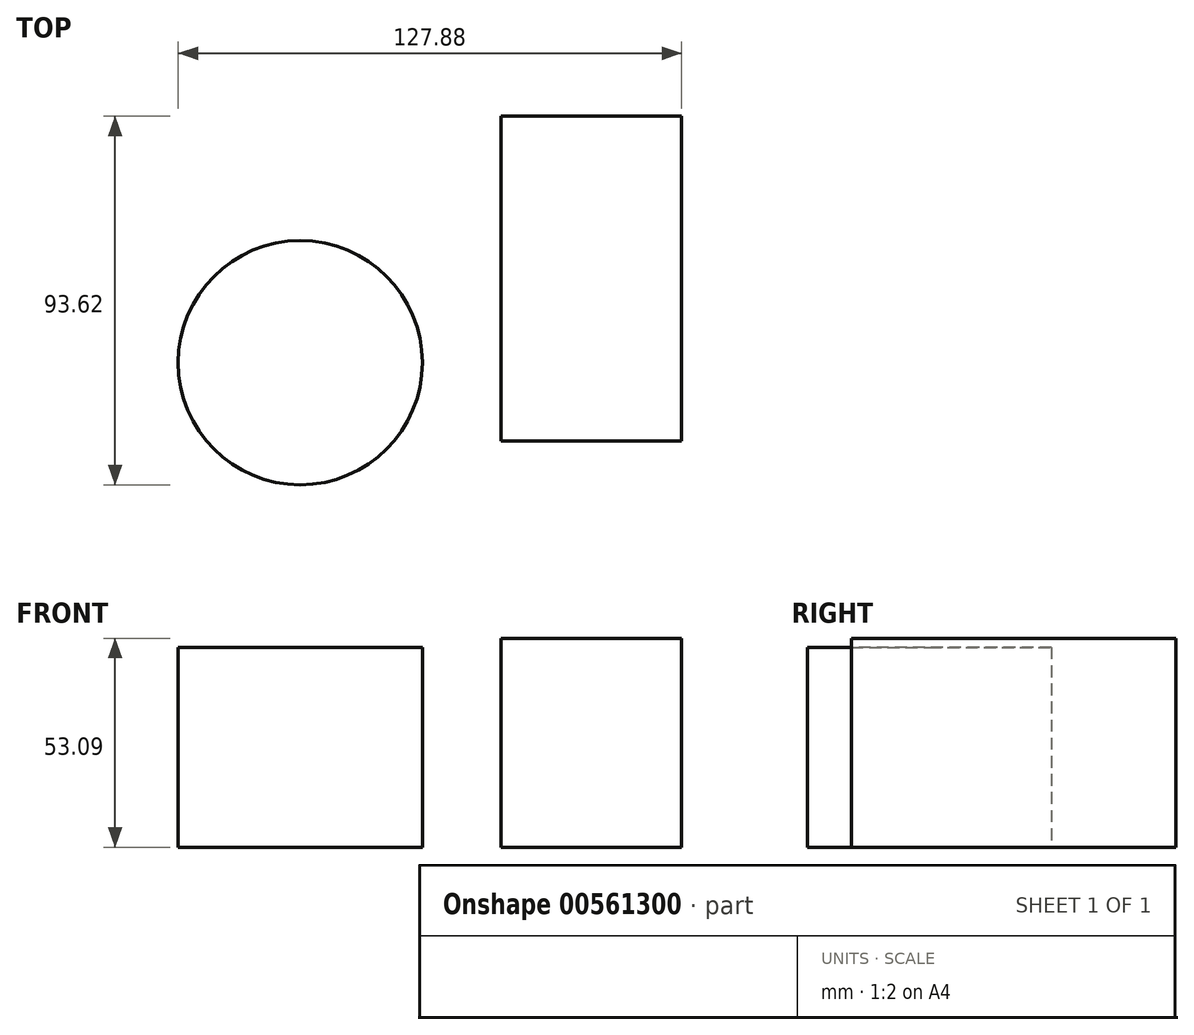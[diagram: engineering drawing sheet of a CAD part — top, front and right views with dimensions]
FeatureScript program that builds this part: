
annotation { "Feature Type Name" : "Feature", "Feature Type Description" : "" }
export const myFeature = defineFeature(function(context is Context, id is Id, definition is map)
    precondition{}
    {
        {
            var Q0;
            Q0=qCreatedBy(makeId("Top.planeOp"),FACE);
            var sketch = newSketch(context, id + "F0", { "sketchPlane" : qUnion([Q0])});
            skCircle(sketch, "E0", {"center": v(-28.08, -21.5) * mm, "radius": 31 * mm});
            skSolve(sketch);
        }
        {
            var Q0;
            Q0 = qSketchRegion(id + "F0", true);
            extrude(context, id + "F1", {"entities" : qUnion([Q0]), "depth" : 50.8 * mm, "offsetDistance" : 25.4 * mm});
        }
        {
            var Q0;
            Q0=qCreatedBy(makeId("Top.planeOp"),FACE);
            var sketch = newSketch(context, id + "F2", { "sketchPlane" : qUnion([Q0])});
            skLineSegment(sketch, "E1.bottom", {"start": v(22.91, -41.37) * mm, "end": v(68.79, -41.37) * mm});
            skLineSegment(sketch, "E1.top", {"start": v(22.91, 41.1) * mm, "end": v(68.79, 41.1) * mm});
            skLineSegment(sketch, "E1.left", {"start": v(22.91, -41.37) * mm, "end": v(22.91, 41.1) * mm});
            skLineSegment(sketch, "E1.right", {"start": v(68.79, -41.37) * mm, "end": v(68.79, 41.1) * mm});
            skSolve(sketch);
        }
        {
            var Q0;
            Q0=makeQuery(id+"F2.imprint","IMPRINT",FACE,{"disambiguationData":[TD([[makeQuery(id+"F2.imprint","IMPRINT",EDGE,{"derivedFrom":sQuery(id+"F2.wireOp",EDGE,"E1.bottom")}),1.0]])]});
            extrude(context, id + "F3", {"entities" : qUnion([Q0]), "depth" : 53.1 * mm, "offsetDistance" : 25.4 * mm});
        }
    });
